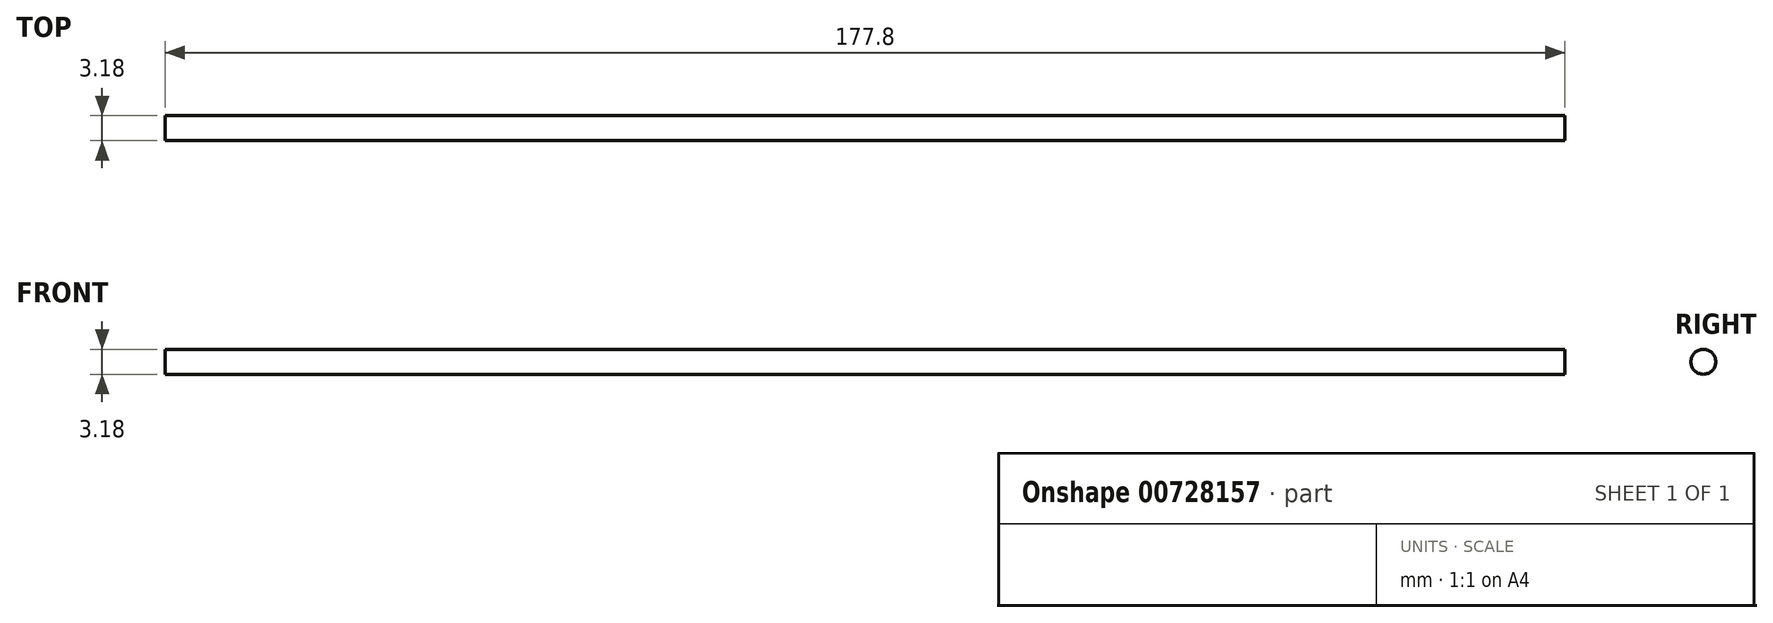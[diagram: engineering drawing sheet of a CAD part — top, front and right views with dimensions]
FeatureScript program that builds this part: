
annotation { "Feature Type Name" : "Feature", "Feature Type Description" : "" }
export const myFeature = defineFeature(function(context is Context, id is Id, definition is map)
    precondition{}
    {
        {
            var Q0;
            Q0=qCreatedBy(makeId("Right.planeOp"),FACE);
            var sketch = newSketch(context, id + "F0", { "sketchPlane" : qUnion([Q0])});
            skCircle(sketch, "E0", {"center": v(0, 0) * mm, "radius": 1.59 * mm});
            skSolve(sketch);
        }
        {
            var Q0;
            Q0=makeQuery(id+"F0.imprint","IMPRINT",FACE,{"disambiguationData":[TD([[makeQuery(id+"F0.imprint","IMPRINT",EDGE,{"derivedFrom":sQuery(id+"F0.wireOp",EDGE,"E0")}),1.0]])]});
            extrude(context, id + "F1", {"entities" : qUnion([Q0]), "depth" : 177.8 * mm, "offsetDistance" : 25.4 * mm});
        }
    });
